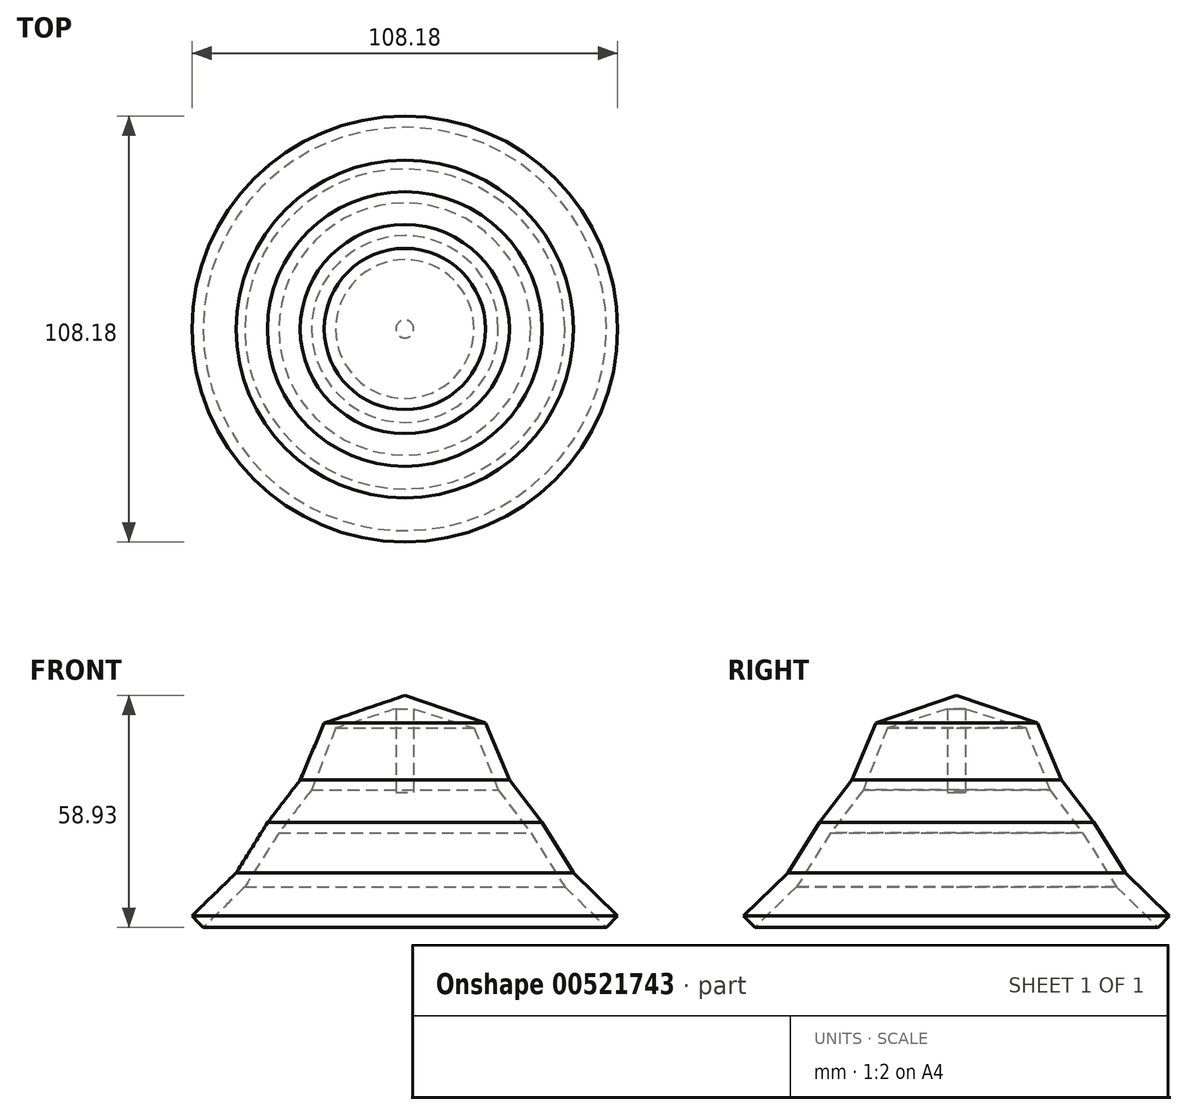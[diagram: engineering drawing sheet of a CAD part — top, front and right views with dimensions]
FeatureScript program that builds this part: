
annotation { "Feature Type Name" : "Feature", "Feature Type Description" : "" }
export const myFeature = defineFeature(function(context is Context, id is Id, definition is map)
    precondition{}
    {
        {
            var Q0;
            Q0=qCreatedBy(makeId("Right.planeOp"),FACE);
            var sketch = newSketch(context, id + "F0", { "sketchPlane" : qUnion([Q0])});
            skLineSegment(sketch, "E0", {"start": v(0, 0) * mm, "end": v(0, 24.64) * mm});
            skLineSegment(sketch, "E1", {"start": v(0, 24.64) * mm, "end": v(20.48, 17.6) * mm});
            skLineSegment(sketch, "E2", {"start": v(20.48, 17.6) * mm, "end": v(26.56, 3.2) * mm});
            skLineSegment(sketch, "E3", {"start": v(26.56, 3.2) * mm, "end": v(34.88, -7.68) * mm});
            skLineSegment(sketch, "E4", {"start": v(34.88, -7.68) * mm, "end": v(42.89, -20.48) * mm});
            skLineSegment(sketch, "E5", {"start": v(42.89, -20.48) * mm, "end": v(54.09, -31.36) * mm});
            skLineSegment(sketch, "E6", {"start": v(54.09, -31.36) * mm, "end": v(51.24, -34.3) * mm});
            skLineSegment(sketch, "E7", {"start": v(51.24, -34.3) * mm, "end": v(40.64, -23.99) * mm});
            skLineSegment(sketch, "E8", {"start": v(40.64, -23.99) * mm, "end": v(32, -10.24) * mm});
            skLineSegment(sketch, "E9", {"start": v(32, -10.24) * mm, "end": v(23.72, 0.6) * mm});
            skLineSegment(sketch, "E10", {"start": v(23.72, 0.6) * mm, "end": v(17.6, 16.33) * mm});
            skLineSegment(sketch, "E11", {"start": v(17.6, 16.33) * mm, "end": v(2.27, 21.24) * mm});
            skLineSegment(sketch, "E12", {"start": v(2.27, 21.24) * mm, "end": v(2.27, 0) * mm});
            skLineSegment(sketch, "E13", {"start": v(2.27, 0) * mm, "end": v(0, 0) * mm});
            skSolve(sketch);
        }
        {
            var Q0;
            Q0 = qSketchRegion(id + "F0", true);
            var Q1;
            Q1=sQuery(id+"F0.wireOp",EDGE,"E0");
            revolve(context, id + "F1", {"entities" : qUnion([Q0]), "axis" : qUnion([Q1]), "revolveType" : RevolveType.FULL});
        }
    });
